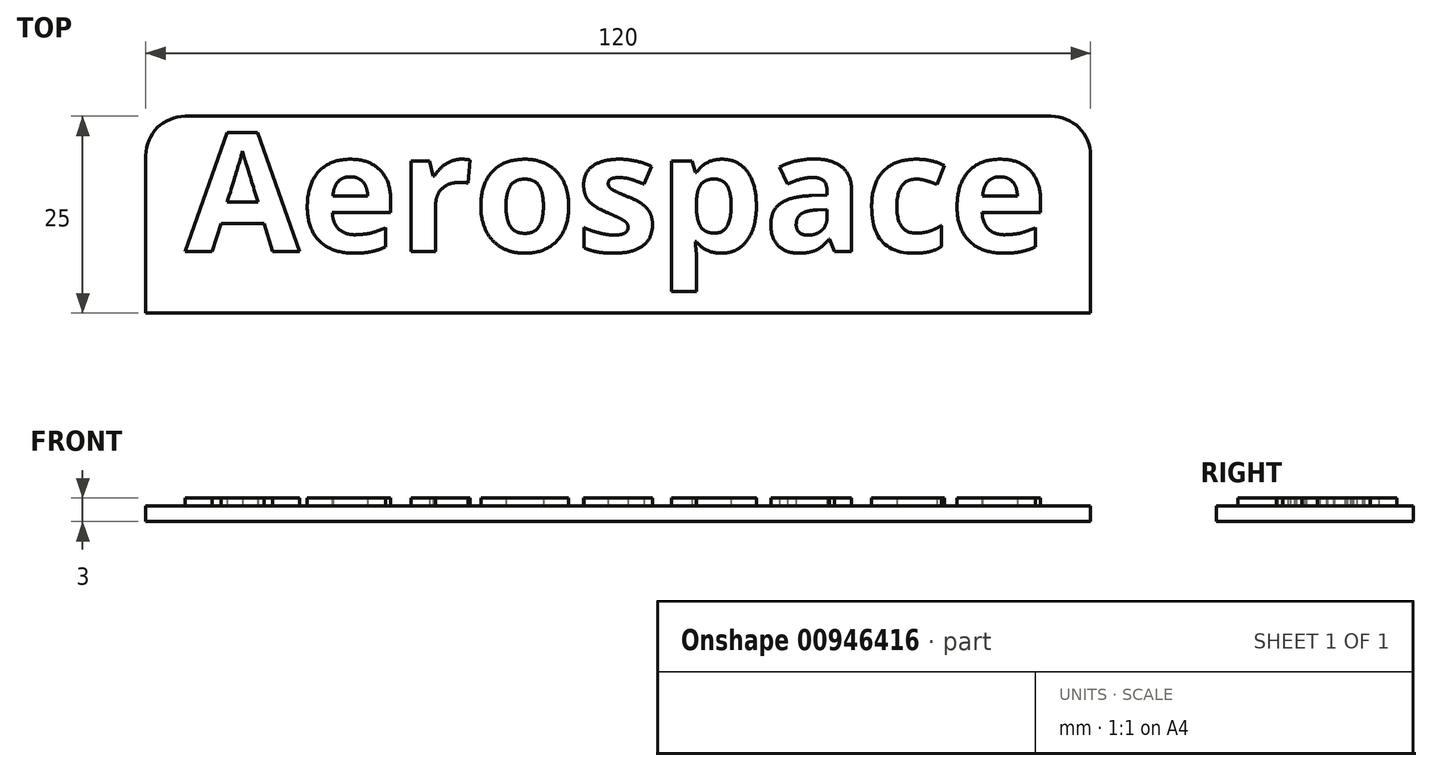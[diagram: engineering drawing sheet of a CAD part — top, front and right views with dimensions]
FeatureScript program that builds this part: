
annotation { "Feature Type Name" : "Feature", "Feature Type Description" : "" }
export const myFeature = defineFeature(function(context is Context, id is Id, definition is map)
    precondition{}
    {
        {
            var Q0;
            Q0=qCreatedBy(makeId("Top.planeOp"),FACE);
            var sketch = newSketch(context, id + "F0", { "sketchPlane" : qUnion([Q0])});
            skLineSegment(sketch, "E0.bottom", {"start": v(-60, 12.5) * mm, "end": v(60, 12.5) * mm});
            skLineSegment(sketch, "E0.top", {"start": v(-60, -12.5) * mm, "end": v(60, -12.5) * mm});
            skLineSegment(sketch, "E0.left", {"start": v(-60, 12.5) * mm, "end": v(-60, -12.5) * mm});
            skLineSegment(sketch, "E0.right", {"start": v(60, 12.5) * mm, "end": v(60, -12.5) * mm});
            skPoint(sketch, "E0.middle", {"position": v(0, 0) * mm});
            skSolve(sketch);
        }
        {
            var Q0;
            Q0=qSketchRegion(id+"F0",true);
            extrude(context, id + "F1", {"entities" : qUnion([Q0]), "depth" : 2 * mm, "offsetDistance" : 25 * mm});
        }
        {
            var Q0;
            Q0=makeQuery(id+"F1.opExtrude","CAP_FACE",FACE,{"disambiguationData":[OSD([sQuery(id+"F0.wireOp",EDGE,"E0.bottom"),sQuery(id+"F0.wireOp",EDGE,"E0.top"),sQuery(id+"F0.wireOp",EDGE,"E0.left"),sQuery(id+"F0.wireOp",EDGE,"E0.right")])],"isStart":false});
            var sketch = newSketch(context, id + "F2", { "sketchPlane" : qUnion([Q0])});
            skText(sketch, "E1", { "text": "Aerospace\n", "fontName": "OpenSans-Bold.ttf"});
            const initialGuessF2  = {"E1": [-0.055, -0.00469, 1, 0, 0.01519]};
            skSetInitialGuess(sketch, initialGuessF2);
            skSolve(sketch);
        }
        {
            var Q0;
            Q0=qSketchRegion(id+"F2",true);
            extrude(context, id + "F3", {"entities" : qUnion([Q0]), "operationType" : NewBodyOperationType.ADD, "depth" : 1 * mm, "offsetDistance" : 25 * mm});
        }
        {
            var Q0;
            Q0=makeQuery(id+"F1.opExtrude","SWEPT_EDGE",EDGE,{"disambiguationData":[OSD([sQuery(id+"F0.wireOp",EDGE,"E0.bottom"),sQuery(id+"F0.wireOp",EDGE,"E0.left")])]});
            var Q1;
            Q1=makeQuery(id+"F1.opExtrude","SWEPT_EDGE",EDGE,{"disambiguationData":[OSD([sQuery(id+"F0.wireOp",EDGE,"E0.bottom"),sQuery(id+"F0.wireOp",EDGE,"E0.right")])]});
            fillet(context, id + "F4", {"entities" : qUnion([Q0, Q1]), "radius" : 5 * mm, "tangentPropagation" : true, "allowEdgeOverflow" : false});
        }
    });
